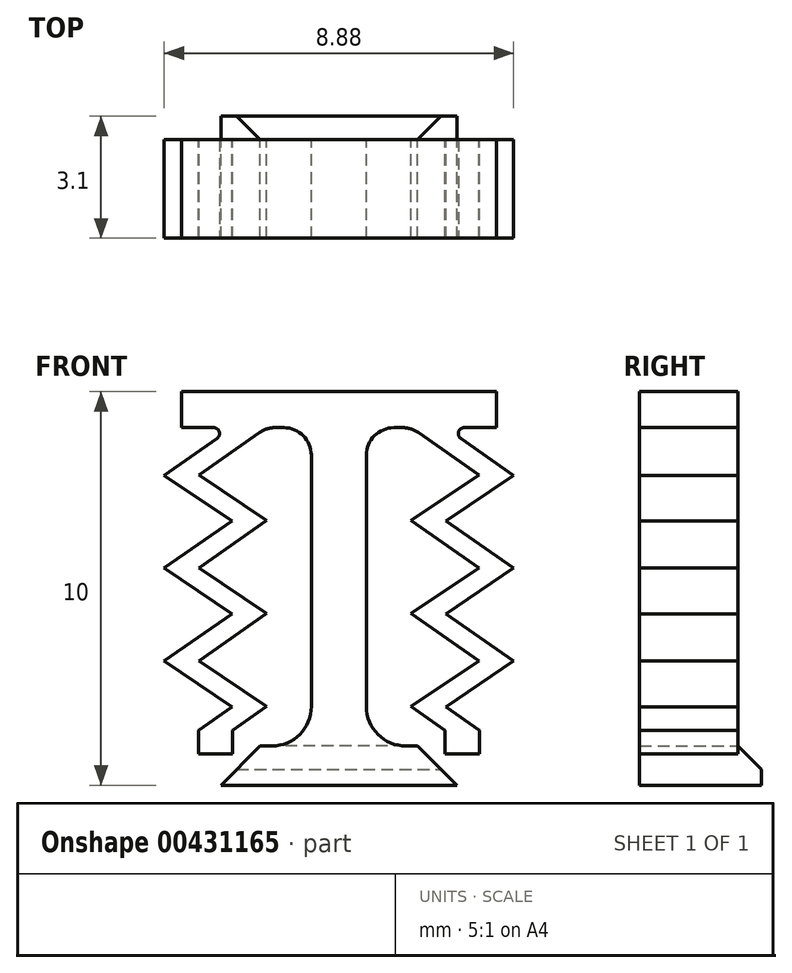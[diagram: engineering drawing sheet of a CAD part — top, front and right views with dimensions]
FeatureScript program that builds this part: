
annotation { "Feature Type Name" : "Feature", "Feature Type Description" : "" }
export const myFeature = defineFeature(function(context is Context, id is Id, definition is map)
    precondition{}
    {
        {
            var Q0;
            Q0=qCreatedBy(makeId("Front.planeOp"),FACE);
            var sketch = newSketch(context, id + "F0", { "sketchPlane" : qUnion([Q0])});
            skLineSegment(sketch, "E0", {"start": v(0, 0) * mm, "end": v(3, 0) * mm});
            skLineSegment(sketch, "E1", {"start": v(3, 0) * mm, "end": v(2, 1) * mm});
            skLineSegment(sketch, "E2", {"start": v(2, 1) * mm, "end": v(0.7, 1) * mm});
            skLineSegment(sketch, "E3", {"start": v(0.7, 1) * mm, "end": v(0.7, 9.09) * mm});
            skLineSegment(sketch, "E4", {"start": v(0, 9) * mm, "end": v(0, 0) * mm});
            skLineSegment(sketch, "E5.top", {"start": v(0, 10) * mm, "end": v(4, 10) * mm});
            skLineSegment(sketch, "E5.left", {"start": v(0, 9) * mm, "end": v(0, 10) * mm});
            skLineSegment(sketch, "E6.bottom", {"start": v(2.7, 0.8) * mm, "end": v(3.57, 0.8) * mm});
            skLineSegment(sketch, "E6.top", {"start": v(2.7, 1.4) * mm, "end": v(3.57, 1.4) * mm});
            skLineSegment(sketch, "E6.left", {"start": v(2.7, 0.8) * mm, "end": v(2.7, 1.4) * mm});
            skLineSegment(sketch, "E6.right", {"start": v(3.57, 0.8) * mm, "end": v(3.57, 1.4) * mm});
            skLineSegment(sketch, "E7", {"start": v(2.7, 1.4) * mm, "end": v(1.84, 2) * mm});
            skLineSegment(sketch, "E8", {"start": v(1.84, 2) * mm, "end": v(3.55, 3.16) * mm});
            skLineSegment(sketch, "E9", {"start": v(3.57, 1.4) * mm, "end": v(2.72, 2) * mm});
            skLineSegment(sketch, "E10", {"start": v(2.72, 2) * mm, "end": v(4.44, 3.16) * mm});
            skLineSegment(sketch, "E11", {"start": v(4.44, 3.16) * mm, "end": v(2.72, 4.36) * mm});
            skLineSegment(sketch, "E12", {"start": v(2.72, 4.36) * mm, "end": v(4.44, 5.52) * mm});
            skLineSegment(sketch, "E13", {"start": v(4.44, 5.52) * mm, "end": v(2.72, 6.72) * mm});
            skLineSegment(sketch, "E14", {"start": v(2.72, 6.72) * mm, "end": v(4.44, 7.88) * mm});
            skLineSegment(sketch, "E15", {"start": v(3.55, 3.16) * mm, "end": v(1.84, 4.37) * mm});
            skLineSegment(sketch, "E16", {"start": v(1.84, 4.37) * mm, "end": v(3.55, 5.52) * mm});
            skLineSegment(sketch, "E17", {"start": v(3.55, 5.52) * mm, "end": v(1.84, 6.73) * mm});
            skLineSegment(sketch, "E18", {"start": v(1.84, 6.73) * mm, "end": v(3.55, 7.88) * mm});
            skLineSegment(sketch, "E19", {"start": v(3.55, 7.88) * mm, "end": v(1.84, 9.09) * mm});
            skLineSegment(sketch, "E20", {"start": v(4.44, 7.88) * mm, "end": v(2.7, 9.09) * mm});
            skLineSegment(sketch, "E21", {"start": v(3.14, 1.4) * mm, "end": v(3.14, 11.55) * mm, "construction": true});
            skLineSegment(sketch, "E22", {"start": v(0.7, 9.09) * mm, "end": v(4, 9.09) * mm});
            skLineSegment(sketch, "E23", {"start": v(4, 9.09) * mm, "end": v(4, 10) * mm});
            skLineSegment(sketch, "E24", {"start": v(0.7, 1) * mm, "end": v(0, 1) * mm});
            skSolve(sketch);
        }
        {
            var Q0;
            Q0=makeQuery(id+"F0.imprint","IMPRINT",FACE,{"disambiguationData":[TD([[makeQuery(id+"F0.imprint","IMPRINT",EDGE,{"derivedFrom":sQuery(id+"F0.wireOp",EDGE,"E0")}),1.0]])]});
            var Q1;
            Q1=makeQuery(id+"F0.imprint","IMPRINT",FACE,{"disambiguationData":[TD([[makeQuery(id+"F0.imprint","IMPRINT",EDGE,{"derivedFrom":sQuery(id+"F0.wireOp",EDGE,"E6.top")}),1.0]])]});
            var Q2;
            Q2=makeQuery(id+"F0.imprint","IMPRINT",FACE,{"disambiguationData":[TD([[makeQuery(id+"F0.imprint","IMPRINT",EDGE,{"derivedFrom":sQuery(id+"F0.wireOp",EDGE,"E6.bottom")}),1.0]])]});
            var Q3;
            {var subQ6=sQuery(id+"F0.wireOp",EDGE,"E3");Q3=makeQuery(id+"F0.imprint","IMPRINT",FACE,{"disambiguationData":[TD([[makeQuery(id+"F0.imprint","IMPRINT",EDGE,{"derivedFrom":subQ6}),1.0]])]});}
            extrude(context, id + "F1", {"entities" : qUnion([Q0, Q1, Q2, Q3]), "depth" : 2.5 * mm});
        }
        {
            var Q0;
            {var subQ1=sQuery(id+"F0.wireOp",EDGE,"E0");Q0=makeQuery(id+"F0.imprint","IMPRINT",FACE,{"disambiguationData":[TD([[makeQuery(id+"F0.imprint","IMPRINT",EDGE,{"derivedFrom":subQ1}),1.0]])]});}
            extrude(context, id + "F2", {"entities" : qUnion([Q0]), "operationType" : NewBodyOperationType.ADD, "oppositeDirection" : true, "depth" : 0.6 * mm});
        }
        {
            var Q0;
            Q0=makeQuery(id+"F1.opExtrude","SWEPT_BODY",BODY,{"disambiguationData":[OSD([sQuery(id+"F0.wireOp",EDGE,"E0"),sQuery(id+"F0.wireOp",EDGE,"E1"),sQuery(id+"F0.wireOp",EDGE,"E2"),sQuery(id+"F0.wireOp",EDGE,"E3"),sQuery(id+"F0.wireOp",EDGE,"6bRmIiaZ-9tWy-Peqi-zsSC-cDDTCut5J2Tu"),sQuery(id+"F0.wireOp",EDGE,"E4")])]});
            var Q1;
            Q1=makeQuery(id+"F1.opExtrude","SWEPT_FACE",FACE,{"disambiguationData":[OSD([sQuery(id+"F0.wireOp",EDGE,"E4")])]});
            mirror(context, id + "F3", {"operationType" : NewBodyOperationType.ADD, "entities" : qUnion([Q0]), "mirrorPlane" : qUnion([Q1])});
        }
        {
            var Q0;
            {var subQ0=makeQuery(id+"F2.opExtrude","CAP_EDGE",EDGE,{"disambiguationData":[OSD([sQuery(id+"F0.wireOp",EDGE,"E2"),sQuery(id+"F0.wireOp",EDGE,"E24")])],"isStart":false});Q0=makeQuery(id+"F3.boolean.opBoolean","MERGE",EDGE,{"derivedFrom":[subQ0,makeQuery(id+"F3.opPattern","COPY",EDGE,{"derivedFrom":subQ0,"instanceName":"1"})]});}
            chamfer(context, id + "F4", {"entities" : qUnion([Q0]), "width" : 0.6 * mm, "tangentPropagation" : true});
        }
        {
            var Q0;
            Q0=makeQuery(id+"F1.opExtrude","SWEPT_EDGE",EDGE,{"disambiguationData":[OSD([sQuery(id+"F0.wireOp",EDGE,"E3"),sQuery(id+"F0.wireOp",EDGE,"E22")])]});
            var Q1;
            Q1=makeQuery(id+"F3.opPattern","COPY",EDGE,{"derivedFrom":makeQuery(id+"F1.opExtrude","SWEPT_EDGE",EDGE,{"disambiguationData":[OSD([sQuery(id+"F0.wireOp",EDGE,"E3"),sQuery(id+"F0.wireOp",EDGE,"E22")])]}),"instanceName":"1"});
            var Q2;
            Q2=makeQuery(id+"F1.opExtrude","SWEPT_EDGE",EDGE,{"disambiguationData":[OSD([sQuery(id+"F0.wireOp",EDGE,"E19"),sQuery(id+"F0.wireOp",EDGE,"E22")])]});
            var Q3;
            Q3=makeQuery(id+"F3.opPattern","COPY",EDGE,{"derivedFrom":makeQuery(id+"F1.opExtrude","SWEPT_EDGE",EDGE,{"disambiguationData":[OSD([sQuery(id+"F0.wireOp",EDGE,"E19"),sQuery(id+"F0.wireOp",EDGE,"E22")])]}),"instanceName":"1"});
            fillet(context, id + "F5", {"entities" : qUnion([Q0, Q1, Q2, Q3]), "radius" : 0.7 * mm, "tangentPropagation" : true, "allowEdgeOverflow" : false});
        }
        {
            var Q0;
            Q0=makeQuery(id+"F1.opExtrude","SWEPT_EDGE",EDGE,{"disambiguationData":[OSD([sQuery(id+"F0.wireOp",EDGE,"E2"),sQuery(id+"F0.wireOp",EDGE,"E3"),sQuery(id+"F0.wireOp",EDGE,"E24")])]});
            var Q1;
            Q1=makeQuery(id+"F3.opPattern","COPY",EDGE,{"derivedFrom":makeQuery(id+"F1.opExtrude","SWEPT_EDGE",EDGE,{"disambiguationData":[OSD([sQuery(id+"F0.wireOp",EDGE,"E2"),sQuery(id+"F0.wireOp",EDGE,"E3"),sQuery(id+"F0.wireOp",EDGE,"E24")])]}),"instanceName":"1"});
            fillet(context, id + "F6", {"entities" : qUnion([Q0, Q1]), "radius" : 1 * mm, "allowEdgeOverflow" : false});
        }
        {
            var Q0;
            Q0=makeQuery(id+"F1.opExtrude","SWEPT_EDGE",EDGE,{"disambiguationData":[OSD([sQuery(id+"F0.wireOp",EDGE,"E20"),sQuery(id+"F0.wireOp",EDGE,"E22")])]});
            var Q1;
            Q1=makeQuery(id+"F3.opPattern","COPY",EDGE,{"derivedFrom":makeQuery(id+"F1.opExtrude","SWEPT_EDGE",EDGE,{"disambiguationData":[OSD([sQuery(id+"F0.wireOp",EDGE,"E20"),sQuery(id+"F0.wireOp",EDGE,"E22")])]}),"instanceName":"1"});
            fillet(context, id + "F7", {"entities" : qUnion([Q0, Q1]), "radius" : 0.15 * mm, "tangentPropagation" : true, "allowEdgeOverflow" : false});
        }
    });
